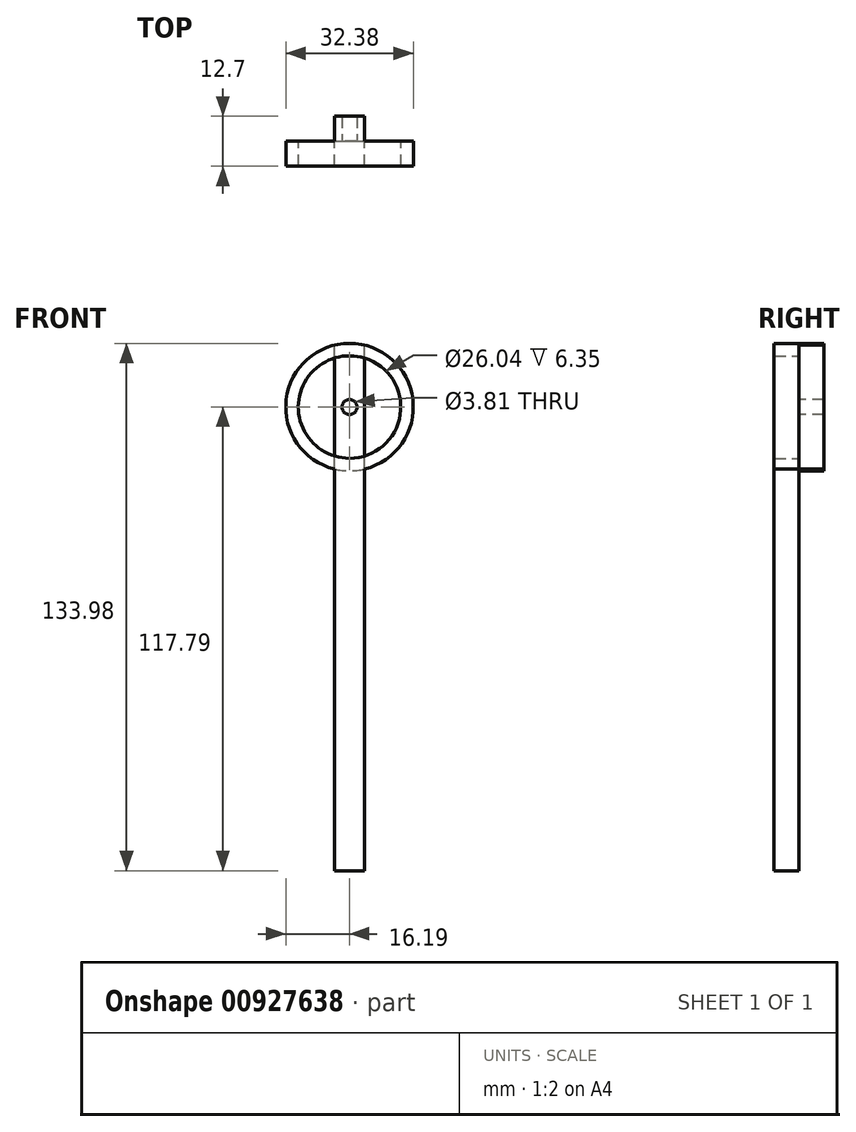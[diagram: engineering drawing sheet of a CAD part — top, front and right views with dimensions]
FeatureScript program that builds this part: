
annotation { "Feature Type Name" : "Feature", "Feature Type Description" : "" }
export const myFeature = defineFeature(function(context is Context, id is Id, definition is map)
    precondition{}
    {
        {
            var Q0;
            Q0=qCreatedBy(makeId("Front.planeOp"),FACE);
            var sketch = newSketch(context, id + "F0", { "sketchPlane" : qUnion([Q0])});
            skArc(sketch, "E0", {"start": v(3.8, -15.74) * mm, "mid": v(0, 16.2) * mm, "end": v(-3.81, -15.74) * mm});
            skArc(sketch, "E1", {"start": v(3.8, -12.45) * mm, "mid": v(0, 13.02) * mm, "end": v(-3.81, -12.45) * mm});
            skLineSegment(sketch, "E2", {"start": v(-3.81, 12.45) * mm, "end": v(-3.81, -12.45) * mm});
            skLineSegment(sketch, "E3", {"start": v(-3.8, -117.8) * mm, "end": v(3.8, -117.8) * mm});
            skLineSegment(sketch, "E4", {"start": v(3.81, -117.8) * mm, "end": v(3.8, -15.74) * mm});
            skCircle(sketch, "E5", {"center": v(0, 0) * mm, "radius": 1.9 * mm});
            skPoint(sketch, "E6.orphan", {"position": v(-3.81, 15.74) * mm});
            skPoint(sketch, "E7.orphan", {"position": v(3.8, 15.74) * mm});
            skLineSegment(sketch, "E8.trimOffspring", {"start": v(-3.81, -15.74) * mm, "end": v(-3.8, -117.8) * mm});
            skLineSegment(sketch, "E9.trimOffspring", {"start": v(3.8, -12.45) * mm, "end": v(3.8, 12.45) * mm});
            skLineSegment(sketch, "E10", {"start": v(-3.81, -15.74) * mm, "end": v(-3.81, -12.45) * mm});
            skLineSegment(sketch, "E11", {"start": v(3.8, -15.74) * mm, "end": v(3.8, -12.45) * mm});
            skCircle(sketch, "E12", {"center": v(0, 0) * mm, "radius": 13.02 * mm});
            skCircle(sketch, "E13", {"center": v(0, 0) * mm, "radius": 16.2 * mm});
            skLineSegment(sketch, "E14", {"start": v(3.8, 12.45) * mm, "end": v(3.8, 15.74) * mm});
            skLineSegment(sketch, "E15", {"start": v(-3.81, 12.45) * mm, "end": v(-3.81, 15.74) * mm});
            skSolve(sketch);
        }
        {
            var Q0;
            Q0=makeQuery(id+"F0.imprint","IMPRINT",FACE,{"disambiguationData":[TD([[makeQuery(id+"F0.imprint","IMPRINT",EDGE,{"derivedFrom":sQuery(id+"F0.wireOp",EDGE,"E3")}),1.0]])]});
            extrude(context, id + "F1", {"entities" : qUnion([Q0]), "depth" : 6.35 * mm, "offsetDistance" : 25.4 * mm});
        }
        {
            var Q0;
            {var subQ0=sQuery(id+"F0.wireOp",EDGE,"E11");Q0=makeQuery(id+"F0.imprint","IMPRINT",FACE,{"disambiguationData":[TD([[makeQuery(id+"F0.imprint","IMPRINT",EDGE,{"derivedFrom":subQ0}),-1.0]])]});}
            var Q1;
            {var subQ0=sQuery(id+"F0.wireOp",EDGE,"E10");Q1=makeQuery(id+"F0.imprint","IMPRINT",FACE,{"disambiguationData":[TD([[makeQuery(id+"F0.imprint","IMPRINT",EDGE,{"derivedFrom":subQ0}),1.0]])]});}
            extrude(context, id + "F2", {"entities" : qUnion([Q0, Q1]), "depth" : 6.35 * mm, "offsetDistance" : 25.4 * mm});
        }
        {
            var Q0;
            {var subQ2=sQuery(id+"F0.wireOp",EDGE,"E14");Q0=makeQuery(id+"F0.imprint","IMPRINT",FACE,{"disambiguationData":[TD([[makeQuery(id+"F0.imprint","IMPRINT",EDGE,{"derivedFrom":subQ2}),1.0]])]});}
            var Q1;
            {var subQ0=sQuery(id+"F0.wireOp",EDGE,"E10");Q1=makeQuery(id+"F0.imprint","IMPRINT",FACE,{"disambiguationData":[TD([[makeQuery(id+"F0.imprint","IMPRINT",EDGE,{"derivedFrom":subQ0}),-1.0]])]});}
            extrude(context, id + "F3", {"entities" : qUnion([Q0, Q1]), "operationType" : NewBodyOperationType.ADD, "endBound" : BoundingType.SYMMETRIC, "depth" : 12.7 * mm, "offsetDistance" : 25.4 * mm});
        }
        {
            var Q0;
            {var subQ1=sQuery(id+"F0.wireOp",EDGE,"E2");Q0=makeQuery(id+"F0.imprint","IMPRINT",FACE,{"disambiguationData":[TD([[makeQuery(id+"F0.imprint","IMPRINT",EDGE,{"derivedFrom":subQ1}),1.0]])]});}
            extrude(context, id + "F4", {"entities" : qUnion([Q0]), "operationType" : NewBodyOperationType.ADD, "oppositeDirection" : true, "depth" : 6.35 * mm, "offsetDistance" : 25.4 * mm});
        }
    });
